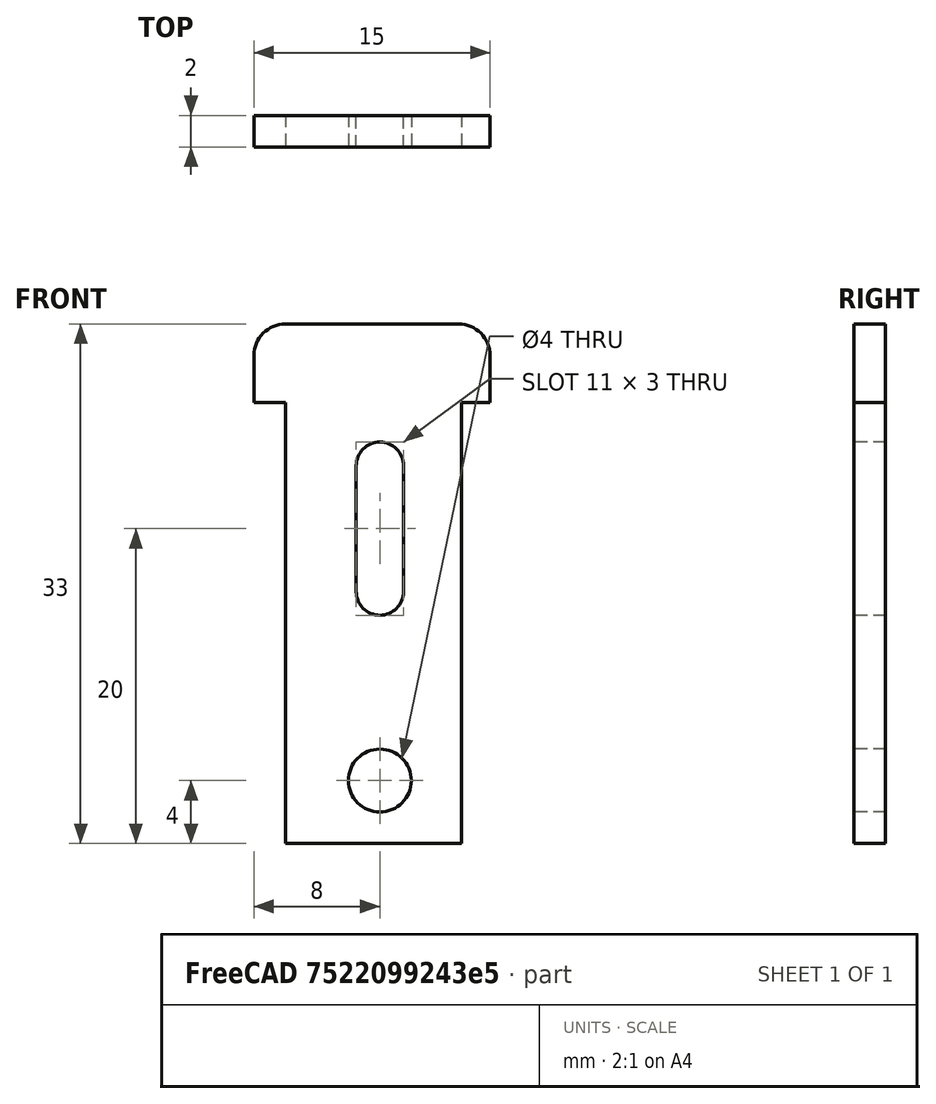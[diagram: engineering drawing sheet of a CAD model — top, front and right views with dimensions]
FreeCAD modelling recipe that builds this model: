
FCSTD DOCUMENT  (FreeCAD 0.17R13541 (Git))
Label: colocador
License: All rights reserved
LicenseURL: http://en.wikipedia.org/wiki/All_rights_reserved
objects: Part::Box×3, Part::Cylinder×3, Part::MultiFuse×2, Part::Cut×1, Part::Fillet×1, Mesh::Feature×1
note: 10 computed .brp shape members not serialized (recipe doc carries the construction recipe); baked Part::Feature solids carry a one-line shape summary decoded from their .brp

FEATURE [Part::Box] Box009  label="Cubo008"
  AttacherType = Attacher::AttachEngine3D
  Height = 8
  Length = 3
  Placement = pos=(86,32,-8) rot=(0,0,1;0rad)
  Width = 10
FEATURE [Part::Cylinder] Cylinder021  label="Cilindro021"
  Angle = 360
  AttacherType = Attacher::AttachEngine3D
  Height = 10
  Placement = pos=(87.5,41.5,0) rot=(1,0,0;1.5708rad)
  Radius = 1.5
FEATURE [Part::Box] Box007  label="Cubo006"
  AttacherType = Attacher::AttachEngine3D
  Height = 30
  Length = 11.2
  Placement = pos=(81.5,35.5,-24) rot=(0,0,1;0rad)
  Width = 2
FEATURE [Part::Cylinder] Cylinder022  label="Cilindro022"
  Angle = 360
  AttacherType = Attacher::AttachEngine3D
  Height = 10
  Placement = pos=(87.5,41.5,-8) rot=(1,0,0;1.5708rad)
  Radius = 1.5
FEATURE [Part::Cylinder] Cylinder023  label="Cilindro023"
  Angle = 360
  AttacherType = Attacher::AttachEngine3D
  Height = 10
  Placement = pos=(87.5,41.5,-20) rot=(1,0,0;1.5708rad)
  Radius = 2
FEATURE [Part::MultiFuse] Fusion006
  Shapes = -> [Box009,Cylinder022,Cylinder021,Cylinder023]
FEATURE [Part::Box] Box008  label="Cubo007"
  AttacherType = Attacher::AttachEngine3D
  Height = 5
  Length = 15
  Placement = pos=(79.5,35.5,4) rot=(0,0,1;0rad)
  Width = 2
FEATURE [Part::MultiFuse] Fusion005
  Shapes = -> [Box007,Box008]
FEATURE [Part::Cut] Cut
  Base = -> Fusion005
  Tool = -> Fusion006
FEATURE [Part::Fillet] Fillet  label="colocador"
  Base = -> Cut
  Edges = 2 edges r=2: [Edge46,Edge47]
FEATURE [Mesh::Feature] Mesh  label="colocador (Meshed)"
